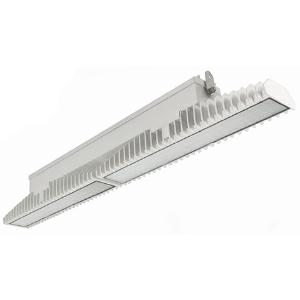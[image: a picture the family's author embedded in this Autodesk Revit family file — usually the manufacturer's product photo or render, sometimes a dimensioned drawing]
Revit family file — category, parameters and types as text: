
# Revit family: 3f_filippi_-_3f_lem_ampio_3f_filippi_-_59161_a0812_-_3f_lem_1_1_led_100-865_cr_ampio___vs_e7b1
name_source: partatom
category: Lighting Fixtures
units: mm (PartAtom-declared; Revit-internal decimal feet)

## family parameters
Cut with Voids When Loaded = No
Host = Face
Light Source = No
Part Type = Normal
Room Calculation Point = No
Round Connector Dimension = Use Diameter
Shared = No

## types (1)
- 3F Filippi - 3F LEM Ampio (1 x LED, 13304 lm, 109 W, 6500 K)
    Apparent Load = 109 VA
    Approval mark = CE
    CIE Flux Codes = 67 90 97 100 100
    Color Rendering = 80
    Color Temperature = 6500 K
    Control Gear = Electronic ballast
    Default Elevation = 1800 mm
    Description = Industrial luminaire with high light output and high luminous efficiency designed with the most innovative technologies for environments with temperature up to 55°C.

ILLUMINOTECHNICAL
Luminous efficiency 100% (DLOR 98%, ULOR 2%).
Initial luminous flux of the luminaire 13304 lm.
Direct symmetric wide distribution: the illuminated area has a rectangular shape.
Installation Interdistance Transv.D = 1.24 x hu - Long.D = 1.20 x hu.
Tabular UGR (CIE 117 - 4H-8H; S=0.25H; 70/50/20): RUG 25.8 - 25.6.
Beam angle: 82° - 83°.
Luminous efficacy 122 lm/W.
Lifetime (L93/B10): 30000 h. (tq+25°C)
Lifetime (L90/B10): 50000 h. (tq+25°C)
Lifetime (L85/B10): 80000 h. (tq+25°C)
Lifetime (L80/B10): 100000 h. (tq+25°C)
Lifetime (L85/B10): 50000 h. (tq+55°C)
Sudden decreased luminous flux after 50000 hours: 0% (C0).
Photobiological safety in compliance with IEC/TR 62778: RG0 risk exempt, (IEC 62471).
In compliance with IEC/EN 62722-2-1 - IEC/EN 62717 standards.

SOURCE
2 Mid-Power linear LED modules 50W/865.
Energy efficiency class (UE 2019/2020 - UE 2019/2015): C.
CIE 13.3 Colour rendering index: CRI >80 (R9 <50%).
IES TM-30 Fidelity Index: Rf = 84 Rg = 95.
CCT nominal colour temperature 6500 K.
Colour initial tolerance (MacAdam): SDCM 3.

MECHANICAL
Passive modular heatsinks in die-casted aluminium, painted in white colour.
To optimize the thermal management of the LED module, the heatsinks are oversized and provided with self-cleaning of cooling fins.
Wiring body in aluminium and galvanised steel anchored solidly to the sinks and thermally separated.
3F Lens lenses with high luminous efficiency, transparent methacrylate (PMMA), fixed to the LED modules.
Fixing brackets in stainless steel.
Luminaire with limited surface temperature. - D - (EN 60598-2-24)
Dimensions: 1099x115 mm, height 154 mm. Weight 11.44 kg.
IP65 protection degree.
Mechanical strength to impacts IK06 (1 joule).
Glow-wire test resistance 650°C.

ELECTRICAL
Halogen Free electronic wiring 230V-50/60Hz, power factor 0.97, THD <25%, constant output current, class I, 1 driver.
Power of the luminaire 109 W.
ENEC - CE.
SAFE FLICKER: PstLM=<1 and SVM=<0.4 (IEC TR 61547-1 and IEC TR 63158), to ensure a more comfortable and safe light.
Luminaire compliant with EN 60598-2-22 for power supply from a centralised emergency system CPSS (Central Power Supply System), not incorporated in the luminaire - high risk areas excluded. The default power and flux are 100% in AC and 100% in DC.
Ambient temperature from -30°C to +55°C.
Temperature class T6 max 85°C.
Quick connection via M20 3P connector with 9-13 mm tightening range.
Power unit positioned on a separate compartment by the LED module to ensure optimum temperatures of cabling components, to be inspectable and maintainable.
Relative humidity UR: <85%.

INSTALLATION
Ceiling / Suspended / Wall.
All accessories dedicated to this product are available on the Catalog and on our website www.3F-Filippi.com.

ACCESSORIES
A0812 - Anti-glare microprismatic VS moulded glass, tempered, not flammable, with sealing gasket.
One required for each light module. The pack contains 10 pieces.

APPLICATIONS
In commercial environments, exhibition and industrial areas, stores, open areas.
Applications with high ambient temperature up to 55°C.
Environments in which it is necessary a total protection against falling fragments (eg environments with foodstuffs or machines with moving parts or with extreme temperature changes), use luminaires with polycarbonate lenses.

WARNING
Fixture not suitable for cold stores with an ambient temperature <0°C and/or relative humidity >85%.
Luminaire designed for disposal/recycling at end-of-life.
Replaceable (LED only) light source by a professional. Replaceable control gear by a professional.
    Height = 154 mm
    Lamp = 1 x LED
    Lamp Light Flux = 13304 lm
    Lamp Power = 109 W
    Lamp count = 1
    Length = 1099 mm
    Lifetime = 50000 h
    Luminous efficacy = 122 lm/W
    Manufacturer = 3F Filippi
    ModVariant = No
    Model = 3F Filippi - 59161+A0812 - 3F LEM 1+1 LED 100-865 CR AMPIO + VS
    Mounting Place = Ceiling
    Mounting Type = Pendant
    Number of Poles = 1
    OnlyDefault = Yes
    Power Factor = 1
    Product Name = 3F Filippi - 3F LEM Ampio
    Product group = pendant luminaire
    ProductGroupID = 9
    Protection Class = Protection class I
    Protection Degree = IP 65
    RLX_Detail_Level = 1
    RLX_Emergency_Light_Flux = 0 lm
    RLX_Emergency_Type = 0
    RLX_Emergency_Type_DB = No
    RlxData = <blob elided: 91121 chars, md5=f21797da>
    Socket = socket
    Standby Power = 0 W
    System Light Flux = 13304 lm
    System Power = 109 W
    Type Comments = Product without accessories
    Type Image = 3f_filippi_-_lem_11__a0812.jpg
    URL = http://relux.com
    VarID = ---
    Voltage = 0 V
    Weight = 0.00 kg
    Width = 115 mm

## geometry (parser evidence)
native form markers: Blend x4, Sweep x14
no freeform markers — native parametric forms only
